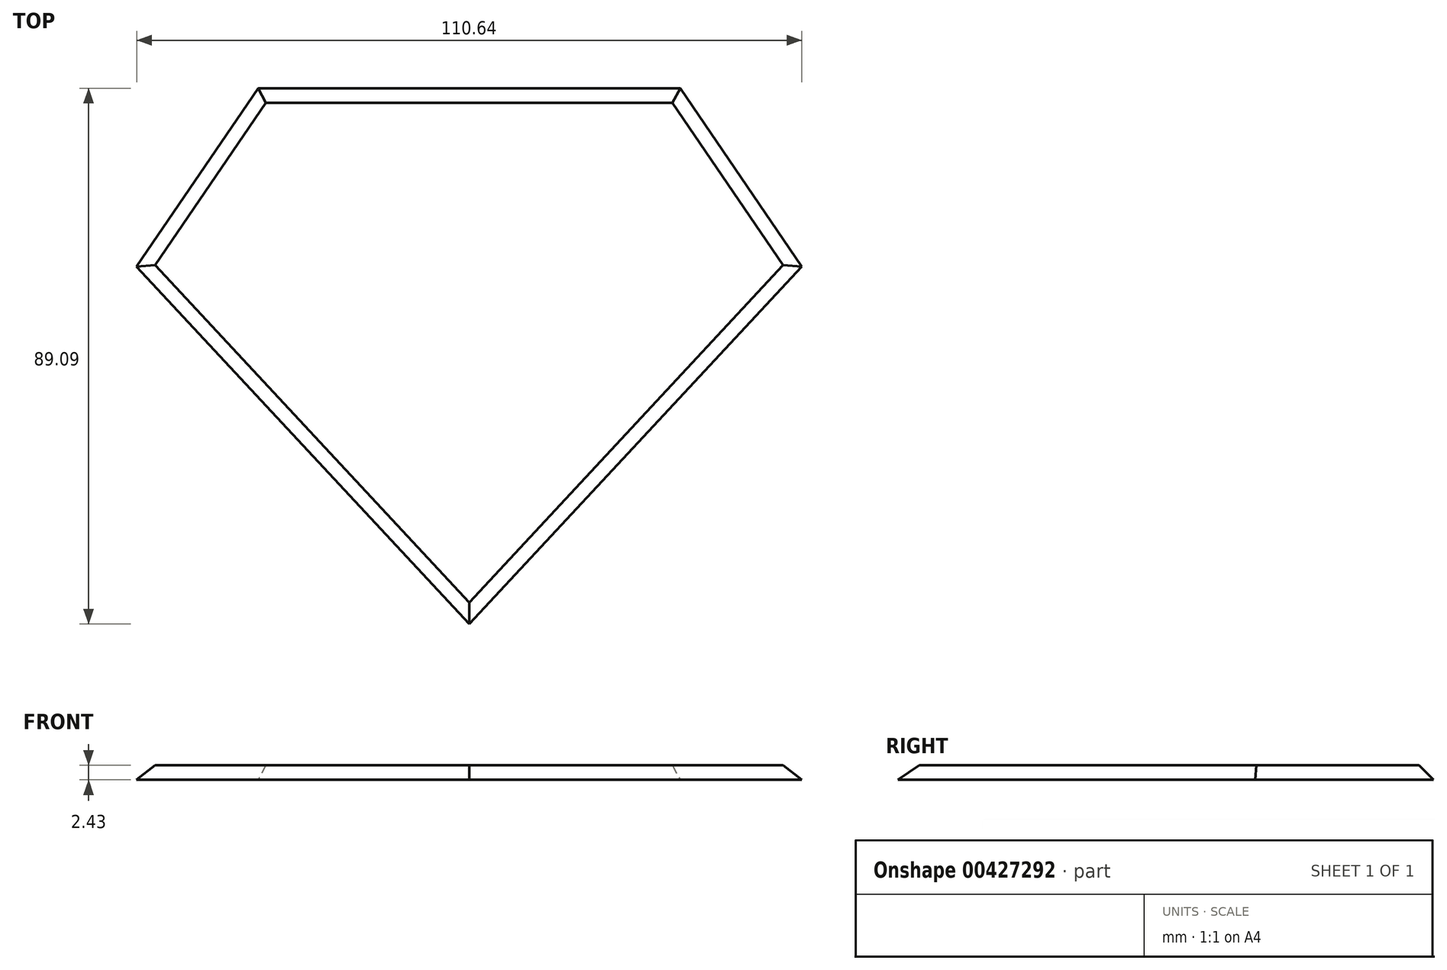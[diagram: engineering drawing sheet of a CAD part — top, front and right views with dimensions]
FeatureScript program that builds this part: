
annotation { "Feature Type Name" : "Feature", "Feature Type Description" : "" }
export const myFeature = defineFeature(function(context is Context, id is Id, definition is map)
    precondition{}
    {
        {
            var Q0;
            Q0=qCreatedBy(makeId("Top.planeOp"),FACE);
            var sketch = newSketch(context, id + "F0", { "sketchPlane" : qUnion([Q0])});
            skLineSegment(sketch, "E0", {"start": v(-36.51, 32.57) * mm, "end": v(0, 32.57) * mm});
            skLineSegment(sketch, "E1", {"start": v(-36.51, 32.57) * mm, "end": v(-58.71, 0) * mm});
            skLineSegment(sketch, "E2", {"start": v(-58.71, 0) * mm, "end": v(0, -63.07) * mm});
            skLineSegment(sketch, "E3", {"start": v(0, 54.56) * mm, "end": v(0, -77.17) * mm});
            skLineSegment(sketch, "E4.MirrorCS", {"start": v(36.51, 32.57) * mm, "end": v(0, 32.57) * mm});
            skLineSegment(sketch, "E5.MirrorCS", {"start": v(36.51, 32.57) * mm, "end": v(58.71, 0) * mm});
            skLineSegment(sketch, "E6.MirrorCS", {"start": v(58.71, 0) * mm, "end": v(0, -63.07) * mm});
            skPoint(sketch, "E7.start.orphan", {"position": v(-40.06, 0) * mm});
            skPoint(sketch, "E8.end.orphan", {"position": v(29.82, 0) * mm});
            skPoint(sketch, "E9.start.orphan", {"position": v(38.53, 0) * mm});
            skSolve(sketch);
        }
        {
            var Q0;
            Q0 = qSketchRegion(id + "F0", true);
            extrude(context, id + "F1", {"entities" : qUnion([Q0]), "depth" : 2.43 * mm});
        }
        {
            var Q0;
            Q0=makeQuery(id+"F1.opExtrude","CAP_EDGE",EDGE,{"disambiguationData":[OSD([sQuery(id+"F0.wireOp",EDGE,"E0"),sQuery(id+"F0.wireOp",EDGE,"E4.MirrorCS")])],"isStart":false});
            chamfer(context, id + "F2", {"entities" : qUnion([Q0]), "width" : 5.08 * mm, "tangentPropagation" : true});
        }
        {
            var Q0;
            Q0=makeQuery(id+"F1.opExtrude","CAP_EDGE",EDGE,{"disambiguationData":[OSD([sQuery(id+"F0.wireOp",EDGE,"E1")])],"isStart":false});
            chamfer(context, id + "F3", {"entities" : qUnion([Q0]), "width" : 5.08 * mm, "tangentPropagation" : true});
        }
        {
            var Q0;
            Q0=makeQuery(id+"F1.opExtrude","CAP_EDGE",EDGE,{"disambiguationData":[OSD([sQuery(id+"F0.wireOp",EDGE,"E5.MirrorCS")])],"isStart":false});
            chamfer(context, id + "F4", {"entities" : qUnion([Q0]), "width" : 5.08 * mm, "tangentPropagation" : true});
        }
        {
            var Q0;
            Q0=makeQuery(id+"F1.opExtrude","CAP_EDGE",EDGE,{"disambiguationData":[OSD([sQuery(id+"F0.wireOp",EDGE,"E6.MirrorCS")])],"isStart":false});
            chamfer(context, id + "F5", {"entities" : qUnion([Q0]), "width" : 5.08 * mm, "tangentPropagation" : true});
        }
        {
            var Q0;
            Q0=makeQuery(id+"F1.opExtrude","CAP_EDGE",EDGE,{"disambiguationData":[OSD([sQuery(id+"F0.wireOp",EDGE,"E2")])],"isStart":false});
            chamfer(context, id + "F6", {"entities" : qUnion([Q0]), "width" : 5.08 * mm, "tangentPropagation" : true});
        }
    });
